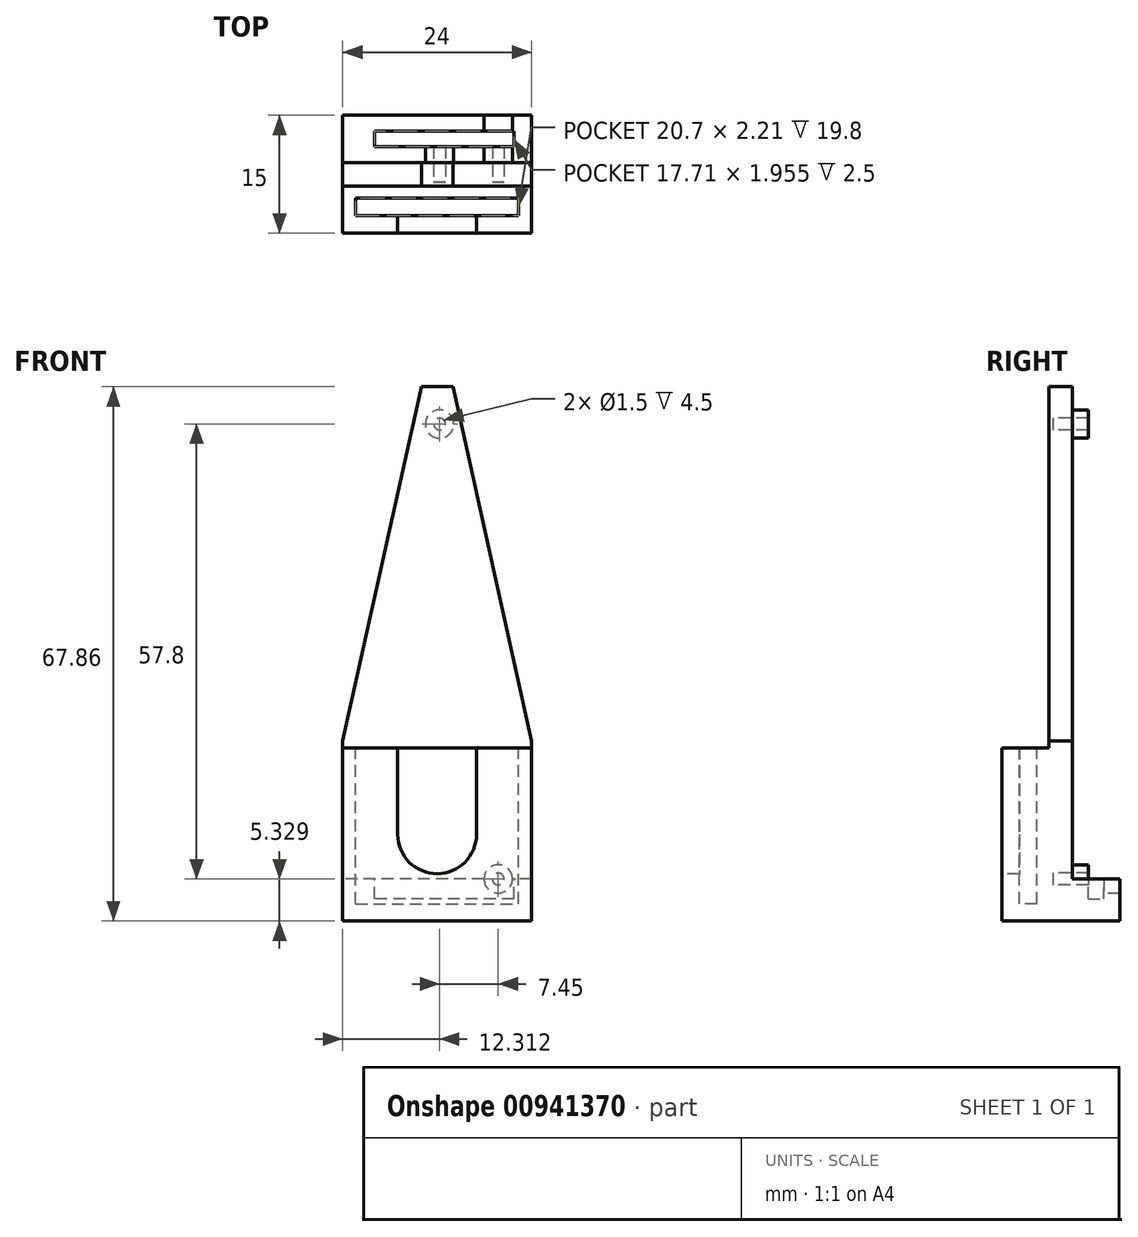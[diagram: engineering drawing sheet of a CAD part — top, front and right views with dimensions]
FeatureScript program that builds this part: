
annotation { "Feature Type Name" : "Feature", "Feature Type Description" : "" }
export const myFeature = defineFeature(function(context is Context, id is Id, definition is map)
    precondition{}
    {
        {
            var Q0;
            Q0=qCreatedBy(makeId("Top.planeOp"),FACE);
            var sketch = newSketch(context, id + "F0", { "sketchPlane" : qUnion([Q0])});
            skLineSegment(sketch, "E0.bottom", {"start": v(-12, 3) * mm, "end": v(12, 3) * mm});
            skLineSegment(sketch, "E0.top", {"start": v(-12, -3) * mm, "end": v(12, -3) * mm});
            skLineSegment(sketch, "E0.left", {"start": v(-12, 3) * mm, "end": v(-12, -3) * mm});
            skLineSegment(sketch, "E0.right", {"start": v(12, 3) * mm, "end": v(12, -3) * mm});
            skSolve(sketch);
        }
        {
            var Q0;
            Q0 = qSketchRegion(id + "F0", true);
            extrude(context, id + "F1", {"entities" : qUnion([Q0]), "depth" : 22 * mm, "offsetDistance" : 25 * mm});
        }
        {
            var Q0;
            Q0=makeQuery(id+"F1.opExtrude","CAP_FACE",FACE,{"disambiguationData":[OSD([sQuery(id+"F0.wireOp",EDGE,"E0.bottom"),sQuery(id+"F0.wireOp",EDGE,"E0.top"),sQuery(id+"F0.wireOp",EDGE,"E0.left"),sQuery(id+"F0.wireOp",EDGE,"E0.right")])],"isStart":false});
            var sketch = newSketch(context, id + "F2", { "sketchPlane" : qUnion([Q0])});
            skLineSegment(sketch, "E1.bottom", {"start": v(-10.35, 1.46) * mm, "end": v(10.35, 1.46) * mm});
            skLineSegment(sketch, "E1.top", {"start": v(-10.35, -0.75) * mm, "end": v(10.35, -0.75) * mm});
            skLineSegment(sketch, "E1.left", {"start": v(-10.35, 1.46) * mm, "end": v(-10.35, -0.75) * mm});
            skLineSegment(sketch, "E1.right", {"start": v(10.35, 1.46) * mm, "end": v(10.35, -0.75) * mm});
            skSolve(sketch);
        }
        {
            var Q0;
            Q0=makeQuery(id+"F2.imprint","IMPRINT",FACE,{"disambiguationData":[TD([[makeQuery(id+"F2.imprint","IMPRINT",EDGE,{"derivedFrom":sQuery(id+"F2.wireOp",EDGE,"E1.bottom")}),-1.0]])]});
            extrude(context, id + "F3", {"entities" : qUnion([Q0]), "operationType" : NewBodyOperationType.REMOVE, "oppositeDirection" : true, "depth" : (18 * 1.1) * mm, "offsetDistance" : 25 * mm});
        }
        {
            var Q0;
            Q0=makeQuery(id+"F1.opExtrude","SWEPT_FACE",FACE,{"disambiguationData":[OSD([sQuery(id+"F0.wireOp",EDGE,"E0.top")])]});
            var sketch = newSketch(context, id + "F4", { "sketchPlane" : qUnion([Q0])});
            skLineSegment(sketch, "E2.0.0", {"start": v(-12, 0) * mm, "end": v(12, 0) * mm, "construction": true});
            skLineSegment(sketch, "E2.0.1", {"start": v(12, 0) * mm, "end": v(12, 22) * mm, "construction": true});
            skLineSegment(sketch, "E2.0.2", {"start": v(12, 22) * mm, "end": v(-12, 22) * mm, "construction": true});
            skLineSegment(sketch, "E2.0.3", {"start": v(-12, 22) * mm, "end": v(-12, 0) * mm, "construction": true});
            skPoint(sketch, "E3", {"position": v(0, 11) * mm});
            skPoint(sketch, "E3.positionSnap0", {"position": v(12, 11) * mm});
            skArc(sketch, "E4", {"start": v(-5, 11) * mm, "mid": v(0, 6) * mm, "end": v(5, 11) * mm});
            skLineSegment(sketch, "E5.bottom", {"start": v(-5, 11) * mm, "end": v(5, 11) * mm});
            skLineSegment(sketch, "E5.top", {"start": v(-5, 22) * mm, "end": v(5, 22) * mm});
            skLineSegment(sketch, "E5.left", {"start": v(-5, 11) * mm, "end": v(-5, 22) * mm});
            skLineSegment(sketch, "E5.right", {"start": v(5, 11) * mm, "end": v(5, 22) * mm});
            skSolve(sketch);
        }
        {
            var Q0;
            Q0=makeQuery(id+"F4.imprint","IMPRINT",FACE,{"disambiguationData":[TD([[makeQuery(id+"F4.imprint","IMPRINT",EDGE,{"derivedFrom":sQuery(id+"F4.wireOp",EDGE,"E5.bottom")}),1.0]])]});
            var Q1;
            Q1=makeQuery(id+"F4.imprint","IMPRINT",FACE,{"disambiguationData":[TD([[makeQuery(id+"F4.imprint","IMPRINT",EDGE,{"derivedFrom":sQuery(id+"F4.wireOp",EDGE,"E4")}),1.0]])]});
            extrude(context, id + "F5", {"entities" : qUnion([Q0, Q1]), "operationType" : NewBodyOperationType.REMOVE, "endBound" : BoundingType.UP_TO_NEXT, "oppositeDirection" : true, "depth" : 25 * mm, "offsetDistance" : 25 * mm});
        }
        {
            var Q0;
            Q0=makeQuery(id+"F1.opExtrude","SWEPT_FACE",FACE,{"disambiguationData":[OSD([sQuery(id+"F0.wireOp",EDGE,"E0.bottom")])]});
            var sketch = newSketch(context, id + "F6", { "sketchPlane" : qUnion([Q0])});
            skLineSegment(sketch, "E6.bottom", {"start": v(-12, 0) * mm, "end": v(12, 0) * mm});
            skLineSegment(sketch, "E6.top", {"start": v(-12, 67.86) * mm, "end": v(12, 67.86) * mm});
            skLineSegment(sketch, "E6.left", {"start": v(-12, 0) * mm, "end": v(-12, 67.86) * mm});
            skLineSegment(sketch, "E6.right", {"start": v(12, 0) * mm, "end": v(12, 67.86) * mm});
            skSolve(sketch);
        }
        {
            var Q0;
            Q0 = qSketchRegion(id + "F6", true);
            extrude(context, id + "F7", {"entities" : qUnion([Q0]), "operationType" : NewBodyOperationType.ADD, "depth" : 3 * mm, "offsetDistance" : 25 * mm});
        }
        {
            var Q0;
            Q0=makeQuery(id+"F7.opExtrude","CAP_FACE",FACE,{"disambiguationData":[OSD([sQuery(id+"F6.wireOp",EDGE,"E6.bottom"),sQuery(id+"F6.wireOp",EDGE,"E6.top"),sQuery(id+"F6.wireOp",EDGE,"E6.left"),sQuery(id+"F6.wireOp",EDGE,"E6.right")])],"isStart":false});
            var sketch = newSketch(context, id + "F8", { "sketchPlane" : qUnion([Q0])});
            skCircle(sketch, "E7", {"center": v(-7.76, 5.33) * mm, "radius": 1.8 * mm});
            skCircle(sketch, "E8", {"center": v(-7.76, 5.33) * mm, "radius": 0.75 * mm});
            skCircle(sketch, "E9", {"center": v(-0.31, 63.13) * mm, "radius": 1.8 * mm});
            skCircle(sketch, "E10", {"center": v(-0.31, 63.13) * mm, "radius": 0.75 * mm});
            skLineSegment(sketch, "E11.bottom", {"start": v(-9.56, 5.33) * mm, "end": v(-5.96, 5.33) * mm});
            skLineSegment(sketch, "E11.top", {"start": v(-9.56, 0) * mm, "end": v(-5.96, 0) * mm});
            skLineSegment(sketch, "E11.left", {"start": v(-9.56, 5.33) * mm, "end": v(-9.56, 0) * mm});
            skLineSegment(sketch, "E11.right", {"start": v(-5.96, 5.33) * mm, "end": v(-5.96, 0) * mm});
            skSolve(sketch);
        }
        {
            var Q0;
            Q0=makeQuery(id+"F8.imprint","IMPRINT",FACE,{"disambiguationData":[TD([[makeQuery(id+"F8.imprint","IMPRINT",EDGE,{"derivedFrom":sQuery(id+"F8.wireOp",EDGE,"E7")}),1.0]])]});
            var Q1;
            Q1=makeQuery(id+"F8.imprint","IMPRINT",FACE,{"disambiguationData":[TD([[makeQuery(id+"F8.imprint","IMPRINT",EDGE,{"derivedFrom":sQuery(id+"F8.wireOp",EDGE,"E9")}),1.0]])]});
            var Q2;
            Q2=makeQuery(id+"F8.imprint","IMPRINT",FACE,{"disambiguationData":[TD([[makeQuery(id+"F8.imprint","IMPRINT",EDGE,{"derivedFrom":sQuery(id+"F8.wireOp",EDGE,"E11.top")}),-1.0]])]});
            extrude(context, id + "F9", {"entities" : qUnion([Q0, Q1, Q2]), "operationType" : NewBodyOperationType.ADD, "depth" : 2 * mm, "offsetDistance" : 25 * mm});
        }
        {
            var Q0;
            Q0=makeQuery(id+"F8.imprint","IMPRINT",FACE,{"disambiguationData":[TD([[makeQuery(id+"F8.imprint","IMPRINT",EDGE,{"derivedFrom":sQuery(id+"F8.wireOp",EDGE,"E8")}),1.0]])]});
            var Q1;
            Q1=makeQuery(id+"F8.imprint","IMPRINT",FACE,{"disambiguationData":[TD([[makeQuery(id+"F8.imprint","IMPRINT",EDGE,{"derivedFrom":sQuery(id+"F8.wireOp",EDGE,"E10")}),1.0]])]});
            extrude(context, id + "F10", {"entities" : qUnion([Q0, Q1]), "operationType" : NewBodyOperationType.REMOVE, "oppositeDirection" : true, "depth" : 2.5 * mm, "offsetDistance" : 25 * mm});
        }
        {
            var Q0;
            Q0=makeQuery(id+"F8.imprint","IMPRINT",FACE,{"disambiguationData":[TD([[makeQuery(id+"F8.imprint","IMPRINT",EDGE,{"derivedFrom":sQuery(id+"F8.wireOp",EDGE,"E9")}),-1.0]])]});
            var sketch = newSketch(context, id + "F11", { "sketchPlane" : qUnion([Q0])});
            skLineSegment(sketch, "E12.0.0", {"start": v(-9.56, 0) * mm, "end": v(-9.56, 5.33) * mm, "construction": true});
            skArc(sketch, "E12.0.1", {"start": v(-9.56, 5.33) * mm, "mid": v(-7.76, 7.13) * mm, "end": v(-5.96, 5.33) * mm, "construction": true});
            skLineSegment(sketch, "E12.0.2", {"start": v(-5.96, 5.33) * mm, "end": v(-5.96, 0) * mm, "construction": true});
            skLineSegment(sketch, "E12.0.3", {"start": v(-5.96, 0) * mm, "end": v(12, 0) * mm, "construction": true});
            skLineSegment(sketch, "E12.0.4", {"start": v(12, 0) * mm, "end": v(12, 67.86) * mm, "construction": true});
            skLineSegment(sketch, "E12.0.5", {"start": v(12, 67.86) * mm, "end": v(-12, 67.86) * mm, "construction": true});
            skLineSegment(sketch, "E12.0.6", {"start": v(-12, 67.86) * mm, "end": v(-12, 0) * mm, "construction": true});
            skLineSegment(sketch, "E12.0.7", {"start": v(-12, 0) * mm, "end": v(-9.56, 0) * mm, "construction": true});
            skLineSegment(sketch, "E13.bottom", {"start": v(-12, 0) * mm, "end": v(12, 0) * mm});
            skLineSegment(sketch, "E13.top", {"start": v(-12, 5.33) * mm, "end": v(12, 5.33) * mm});
            skLineSegment(sketch, "E13.left", {"start": v(-12, 0) * mm, "end": v(-12, 5.33) * mm});
            skLineSegment(sketch, "E13.right", {"start": v(12, 0) * mm, "end": v(12, 5.33) * mm});
            skCircle(sketch, "E14.0", {"center": v(-7.76, 5.33) * mm, "radius": 1.8 * mm});
            skSolve(sketch);
        }
        {
            var Q0;
            {var subQ0=sQuery(id+"F11.wireOp",EDGE,"E13.left");Q0=makeQuery(id+"F11.imprint","IMPRINT",FACE,{"disambiguationData":[TD([[makeQuery(id+"F11.imprint","IMPRINT",EDGE,{"derivedFrom":subQ0}),1.0]])]});}
            var Q1;
            {var subQ0=sQuery(id+"F11.wireOp",EDGE,"E13.right");Q1=makeQuery(id+"F11.imprint","IMPRINT",FACE,{"disambiguationData":[TD([[makeQuery(id+"F11.imprint","IMPRINT",EDGE,{"derivedFrom":subQ0}),-1.0]])]});}
            var Q2;
            Q2=makeQuery(id+"F8.imprint","IMPRINT",FACE,{"disambiguationData":[TD([[makeQuery(id+"F8.imprint","IMPRINT",EDGE,{"derivedFrom":sQuery(id+"F8.wireOp",EDGE,"E11.top")}),-1.0]])]});
            extrude(context, id + "F12", {"entities" : qUnion([Q0, Q1, Q2]), "operationType" : NewBodyOperationType.ADD, "depth" : 6 * mm, "offsetDistance" : 25 * mm});
        }
        {
            var Q0;
            {var subQ0=sQuery(id+"F11.wireOp",EDGE,"E13.top");Q0=makeQuery(id+"F12.opExtrude","SWEPT_FACE",FACE,{"disambiguationData":[OSD([subQ0]),TDD([makeQuery(id+"F11.imprint","IMPRINT",EDGE,{"disambiguationData":[TD([[makeQuery(id+"F11.imprint","INTERSECT",VERTEX,{"derivedFrom":[makeQuery(id+"F8.imprint","IMPRINT",EDGE,{"derivedFrom":sQuery(id+"F8.wireOp",EDGE,"E11.right")}),subQ0]}),-1.0]])],"derivedFrom":subQ0})])]});}
            var sketch = newSketch(context, id + "F13", { "sketchPlane" : qUnion([Q0])});
            skLineSegment(sketch, "E15.0.1", {"start": v(5.96, 8) * mm, "end": v(9.56, 8) * mm, "construction": true});
            skLineSegment(sketch, "E16.bottom", {"start": v(9.76, 8) * mm, "end": v(-7.95, 8) * mm});
            skLineSegment(sketch, "E16.top", {"start": v(9.76, 9.95) * mm, "end": v(-7.95, 9.95) * mm});
            skLineSegment(sketch, "E16.left", {"start": v(9.76, 8) * mm, "end": v(9.76, 9.95) * mm});
            skLineSegment(sketch, "E16.right", {"start": v(-7.95, 8) * mm, "end": v(-7.95, 9.95) * mm});
            skLineSegment(sketch, "E17.0", {"start": v(7.01, 8) * mm, "end": v(8.51, 8) * mm});
            skPoint(sketch, "E18", {"position": v(7.76, 8) * mm});
            skSolve(sketch);
        }
        {
            var Q0;
            {var subQ0=sQuery(id+"F13.wireOp",EDGE,"E16.right");Q0=makeQuery(id+"F13.imprint","IMPRINT",FACE,{"disambiguationData":[TD([[makeQuery(id+"F13.imprint","IMPRINT",EDGE,{"derivedFrom":subQ0}),-1.0]])]});}
            var Q1;
            {var subQ0=sQuery(id+"F13.wireOp",EDGE,"E16.left");Q1=makeQuery(id+"F13.imprint","IMPRINT",FACE,{"disambiguationData":[TD([[makeQuery(id+"F13.imprint","IMPRINT",EDGE,{"derivedFrom":subQ0}),1.0]])]});}
            extrude(context, id + "F14", {"entities" : qUnion([Q0, Q1]), "operationType" : NewBodyOperationType.REMOVE, "oppositeDirection" : true, "depth" : 2.5 * mm, "offsetDistance" : 25 * mm});
        }
        {
            var Q0;
            Q0=makeQuery(id+"F7.opExtrude","SWEPT_EDGE",EDGE,{"disambiguationData":[OSD([sQuery(id+"F6.wireOp",EDGE,"E6.top"),sQuery(id+"F6.wireOp",EDGE,"E6.right")])]});
            var Q1;
            Q1=makeQuery(id+"F7.opExtrude","SWEPT_EDGE",EDGE,{"disambiguationData":[OSD([sQuery(id+"F6.wireOp",EDGE,"E6.top"),sQuery(id+"F6.wireOp",EDGE,"E6.left")])]});
            chamfer(context, id + "F15", {"entities" : qUnion([Q0, Q1]), "chamferType" : ChamferType.TWO_OFFSETS, "width1" : 10 * mm, "oppositeDirection" : false, "width2" : 45 * mm, "tangentPropagation" : true});
        }
    });
